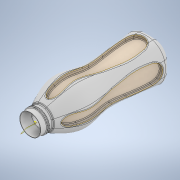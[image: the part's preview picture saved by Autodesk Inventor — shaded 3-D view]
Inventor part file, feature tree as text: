
AUTODESK INVENTOR PART (.ipt)
format: ipt  version: 2021 (Build 250183000, 183)  size: 10,690,048 bytes
history: native  units: mm
features: sketch x12, plane x8, other x6, fillet x5, thicken_offset x4, surface_op x4, extrude x2, loft x1, pattern_circular x1, shell x1, sweep x1
ambient origin geometry x8: Origin, YZ Plane, XZ Plane, XY Plane, X Axis, Y Axis, Z Axis, Center Point
bodies: Solid1 (feature_tree), Solid2 (feature_tree)
feature tree (45):
  sketch  "Sketch1"  dims[d0=80.0mm d1=80.0mm d2=25.0mm]
  plane  "Work Plane1"
  sketch  "Sketch2"  dims[d3=25.0mm d4=25.0mm d5=25.0mm]
  plane  "Work Plane2"
  sketch  "Sketch4"  dims[d6=35.0mm d7=85.0mm d8=80.0mm]
  plane  "Work Plane3"
  sketch  "Sketch5"  dims[d9=75.0mm]
  plane  "Work Plane4"
  sketch  "Sketch6"  dims[d10=65.0mm d11=90.0mm d12=45.0mm d13=55.0mm d14=5.0mm]
  plane  "Work Plane5"
  loft  "Loft1"
  fillet  "Fillet1"  Radius=25.0mm
  extrude  "Extrusion1"  Depth=25.0mm
  fillet  "Fillet2"  Radius=25.0mm
  extrude  "Extrusion2"  Depth=85.0mm
  fillet  "Fillet3"  Radius=80.0mm
  plane  "Work Plane6"
  sketch  "Sketch13"  dims[d20=0.0mm d21=90.0deg]
  pattern_circular  "Circular Pattern1"  Count=9  [1 undecoded]
  thicken_offset  "Thicken1"
  thicken_offset  "Thicken2"
  thicken_offset  "Thicken3"
  thicken_offset  "Thicken4"
  fillet  "Fillet4"  Radius=45.0mm
  fillet  "Fillet5"  Radius=55.0mm
  shell  "Shell1"  Thickness=5.0mm
  plane  "Work Plane7"
  sketch  "Sketch14"  dims[d22=0.0mm d23=90.0deg]
  sketch  "3D Sketch2"
  plane  "Work Plane10"
  sweep  "Sweep1"
  sketch  "Sketch7"  dims[d15=50.0mm d16=0.0mm d17=90.0deg]
  sketch  "Sketch12"  dims[d18=0.0mm d19=90.0deg]
  sketch  "3D Sketch1"
  other  "Project to Surface1"
  other  "Srf1"
  other  "Srf2"
  other  "Srf3"
  other  "Srf4"
  other  "Helical Curve1"
  sketch  "Sketch17"  dims[d24=0.0mm d25=90.0deg d26=0.0mm d27=90.0deg d28=10.0mm d31=5.0mm d32=0.0mm d33=2.5mm d34=45.0mm d35=25.0mm d36=0.0mm d37=2.0mm d38=87.75mm d39=160.0mm d40=15.0mm d42=40.0mm d43=22.0mm d44=11.0mm d47=180.0mm d48=500.0mm d49=22.0mm d50=0.0mm d51=40.0mm d52=360.0deg d54=15.0mm d55=15.0mm d56=15.0mm d57=15.0mm d58=15.0mm d59=15.0mm d60=15.0mm d61=15.0mm d62=1.5mm d63=1.5mm d64=1.0mm d65=-10.0mm d66=8.0mm d67=20.0mm d68=45.0mm d69=0.0mm d72=-10.0mm d74=0.0mm d75=0.0mm]
  surface_op  "Boundary Patch1"
  surface_op  "Boundary Patch2"
  surface_op  "Boundary Patch3"
  surface_op  "Boundary Patch4"
note: 1 required parameter value undecoded (feature->parameter linkage not recoverable at this tier; creation-order binding heuristic only, values carry confidence <= 0.55)
